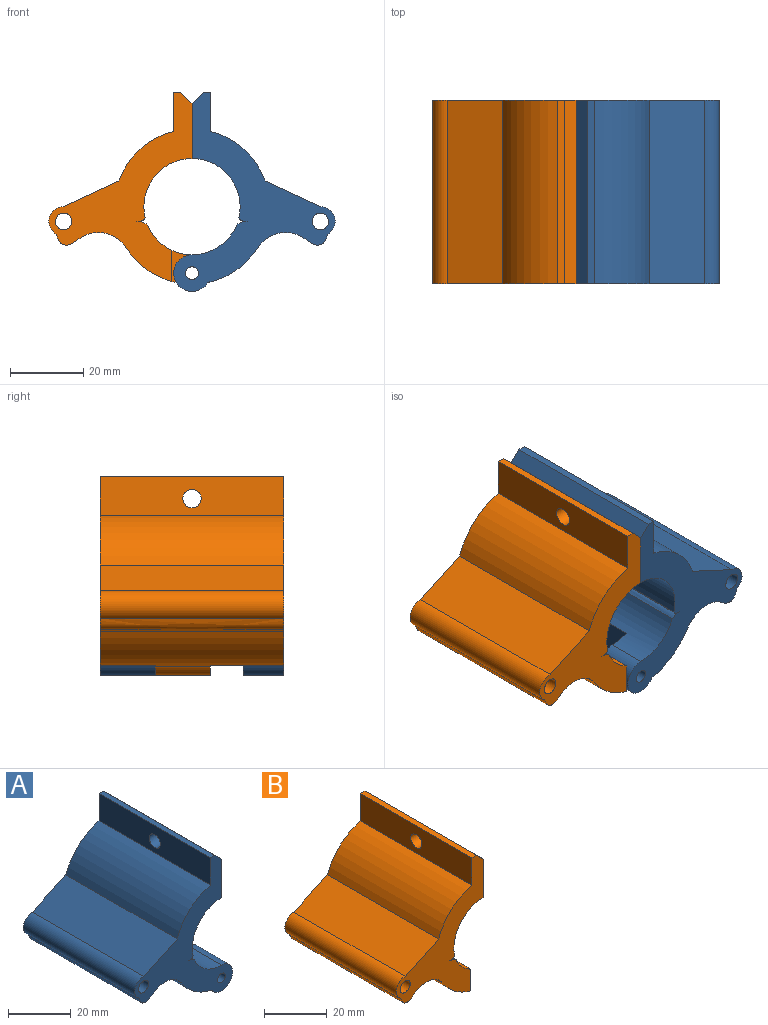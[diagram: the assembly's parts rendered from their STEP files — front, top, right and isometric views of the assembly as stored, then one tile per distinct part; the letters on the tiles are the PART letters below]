
ASSEMBLY  parts=2 mates=1
PART A: 25 faces, bbox 44x50x54.2 mm
  f0: cylinder r=5mm len=15mm, axis (0,1,0), area 313.1mm2, adj f2,f14,f16,f19
  f1: cylinder r=5mm len=11mm, axis (0,1,0), area 229.6mm2, adj f2,f14,f17,f20
  f2: cylinder r=13.12mm len=50mm, axis (0,1,0), area 640.8mm2, adj f0,f1,f3,f16,f17,f18,f19,f20
  f3: extruded ~50x2.87mm, area 155.1mm2, adj f2,f4,f16,f17
  f4: extruded ~50x2.22mm, area 132.2mm2, adj f3,f5,f16,f17
  f5: cylinder r=13.12mm len=50mm, axis (0,1,0), area 1182.1mm2, adj f4,f6,f16,f17
  f6: plane 50x15mm, normal (1,0,0), area 730.4mm2, adj f5,f16,f17,f23,f24
  f7: plane 50x2mm, normal (0,0,1), area 100mm2, adj f8,f16,f17,f24
  f8: plane 50x10.6mm, normal (-1,0,0), area 510.4mm2, adj f7,f9,f16,f17,f23
  f9: cylinder r=21.12mm len=50mm, axis (0,1,0), area 1050mm2, adj f8,f10,f16,f17
  f10: plane 50x15.07mm, normal (-0.42,0,0.91), area 830.8mm2, adj f9,f11,f16,f17
  f11: cylinder r=4mm len=50mm, axis (0,1,0), area 523.6mm2, adj f10,f12,f16,f17
  f12: extruded ~50x5.91mm, area 397.6mm2, adj f11,f13,f16,f17
  f13: cylinder r=9mm len=50mm, axis (0,1,0), area 745.2mm2, adj f12,f14,f16,f17
  f14: cylinder r=21.12mm len=50mm, axis (0,1,0), area 833.8mm2, adj f0,f1,f13,f16,f17,f18,f19,f20
  f15: cylinder r=2.25mm len=50mm, axis (0,1,0), area 706.9mm2, adj f16,f17
  f16: plane 54.25x44mm, normal (0,-1,0), area 691.1mm2, adj f0,f2,f3,f4,f5,f6,f7,f8
  f17: plane 54.25x44mm, normal (0,1,0), area 691.1mm2, adj f1,f2,f3,f4,f5,f6,f7,f8
  f18: plane 24x8.46mm, normal (1,0,0), area 203mm2, adj f2,f14,f19,f20
  f19: plane 11.16x10.4mm, normal (0,1,0), area 79.8mm2, adj f0,f2,f14,f18,f22
  f20: plane 11.16x10.4mm, normal (0,-1,0), area 79.8mm2, adj f1,f2,f14,f18,f21
  f21: cylinder r=1.75mm len=11mm, axis (0,-1,0), area 121mm2, adj f17,f20
  f22: cylinder r=1.75mm len=15mm, axis (0,-1,0), area 164.9mm2, adj f16,f19
  f23: cylinder r=2.5mm len=5mm, axis (1,0,0), area 78.5mm2, adj f6,f8
  f24: plane 50x3mm, normal (0.71,0,0.71), area 212.1mm2, adj f6,f7,f16,f17
PART B: 24 faces, bbox 44x50x54.2 mm
  f0: cylinder r=5mm len=15mm, axis (0,1,0), area 313.1mm2, adj f1,f2,f18,f20
  f1: cylinder r=13.12mm len=50mm, axis (0,1,0), area 575.8mm2, adj f0,f3,f15,f16,f17,f18,f19,f20
  f2: cylinder r=21.12mm len=50mm, axis (0,1,0), area 817.8mm2, adj f0,f13,f15,f16,f17,f18,f19,f20
  f3: extruded ~50x2.87mm, area 155.1mm2, adj f1,f4,f15,f16
  f4: extruded ~50x2.22mm, area 132.2mm2, adj f3,f5,f15,f16
  f5: cylinder r=13.12mm len=50mm, axis (0,1,0), area 1182.1mm2, adj f4,f6,f15,f16
  f6: plane 50x15mm, normal (1,0,0), area 730.4mm2, adj f5,f15,f16,f22,f23
  f7: plane 50x2mm, normal (0,0,1), area 100mm2, adj f8,f15,f16,f23
  f8: plane 50x10.6mm, normal (-1,0,0), area 510.4mm2, adj f7,f9,f15,f16,f22
  f9: cylinder r=21.12mm len=50mm, axis (0,1,0), area 1050mm2, adj f8,f10,f15,f16
  f10: plane 50x15.07mm, normal (-0.42,0,0.91), area 830.8mm2, adj f9,f11,f15,f16
  f11: cylinder r=4mm len=50mm, axis (0,1,0), area 523.6mm2, adj f10,f12,f15,f16
  f12: extruded ~50x5.91mm, area 397.6mm2, adj f11,f13,f15,f16
  f13: cylinder r=9mm len=50mm, axis (0,1,0), area 745.2mm2, adj f2,f12,f15,f16
  f14: cylinder r=2.25mm len=50mm, axis (0,1,0), area 706.9mm2, adj f15,f16
  f15: plane 51.52x39mm, normal (0,-1,0), area 610.5mm2, adj f1,f2,f3,f4,f5,f6,f7,f8
  f16: plane 51.52x39mm, normal (0,1,0), area 610.5mm2, adj f1,f2,f3,f4,f5,f6,f7,f8
  f17: plane 15x8.48mm, normal (1,0,0), area 127.2mm2, adj f1,f2,f16,f18
  f18: plane 11.21x10.5mm, normal (0,1,0), area 77.7mm2, adj f0,f1,f2,f17,f21
  f19: plane 20x8.48mm, normal (1,0,0), area 169.6mm2, adj f1,f2,f15,f20
  f20: plane 11.21x10.5mm, normal (0,-1,0), area 77.7mm2, adj f0,f1,f2,f19,f21
  f21: cylinder r=2mm len=15mm, axis (0,1,0), area 188.5mm2, adj f18,f20
  f22: cylinder r=2.5mm len=5mm, axis (1,0,0), area 78.5mm2, adj f6,f8
  f23: plane 50x3mm, normal (0.71,0,0.71), area 212.1mm2, adj f6,f7,f15,f16
PLACE A rot(axis=(0,0,1),180deg) t=(-37.53,-21.29,-0.6)mm
PLACE B rot(axis=(0,0,1),0deg) t=(-73.53,28.71,-0.6)mm
MATE fastened A.f23 <-> B.f22  axis (-1,0,0) through (-55.53,3.71,28.53)mm
